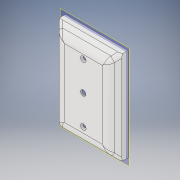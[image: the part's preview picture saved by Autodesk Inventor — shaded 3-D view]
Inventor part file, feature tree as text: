
AUTODESK INVENTOR PART (.ipt)
format: ipt  version: 2018 (Build 220112000, 112)  size: 312,832 bytes
history: native  units: in
note: dims shown in document units (in); Inventor stores cm internally (conversion verified against a paired STEP export)
features: reference x7, other x6, extrude x5, sketch x5, chamfer x2, fillet x2, shell x1, plane x1
ambient origin geometry x8: Origin, YZ Plane, XZ Plane, XY Plane, X Axis, Y Axis, Z Axis, Center Point
bodies: Body1 (feature_tree)
feature tree (29):
  extrude  "Extrusion5"  Depth=0.4in TaperAngle=45.0deg
  chamfer  "Chamfer1"  Distance=0.1575in
  fillet  "Fillet3"  Radius=0.1575in
  fillet  "Fillet4"  Radius=0.75in
  shell  "Shell1"  Thickness=3.5in
  extrude  "Extrusion6"  Depth=0.315in
  plane  "Work Plane3"
  extrude  "Extrusion8"  Depth=0.315in
  extrude  "Extrusion10"  [1 undecoded]
  chamfer  "Chamfer3"  Distance=0.25in
  extrude  "Extrusion11"  Depth=0.315in
  sketch  "Sketch5"  dims[d67=0.75in d68=0.0in d69=0.4in d70=0.125in d71=45.0deg]
  sketch  "Sketch6"  dims[d72=0.7in]
  reference  "Reference5"
  reference  "Reference6"
  reference  "Reference7"
  reference  "Reference12"
  sketch  "Sketch9"  dims[d73=0.3in]
  reference  "Reference13"
  reference  "Reference15"
  reference  "Reference16"
  sketch  "Sketch10"  dims[d74=0.0827in]
  sketch  "Sketch11"  dims[d75=0.3in d77=0.1575in d78=0.1575in d79=0.75in d80=0.0in d93=3.5in d94=5.2in d95=1.75in d96=-0.1181in d97=0.25in d99=0.25in d100=0.25in d101=0.5143in d102=0.0in d103=0.0984in d105=0.0984in d106=0.0984in d109=0.3in d110=0.0in d111=0.0787in d112=0.125in d113=45.0deg d114=0.4724in d115=0.0827in d116=0.5in d117=0.315in d118=0.0in]
  other  "<userpath>\Desktop\LocalGit\seniorproject\hardware\mechanical\LightSwitchAssembly.iam"
  other  "LightSwitchAssembly.iam"
  other  "LightSwitch:1"
  other  "EncoderDaughter:1"
  other  "S1_3"
  other  "pec11r-4215k-n0024_2"
note: 1 required parameter value undecoded (feature->parameter linkage not recoverable at this tier; creation-order binding heuristic only, values carry confidence <= 0.55)
